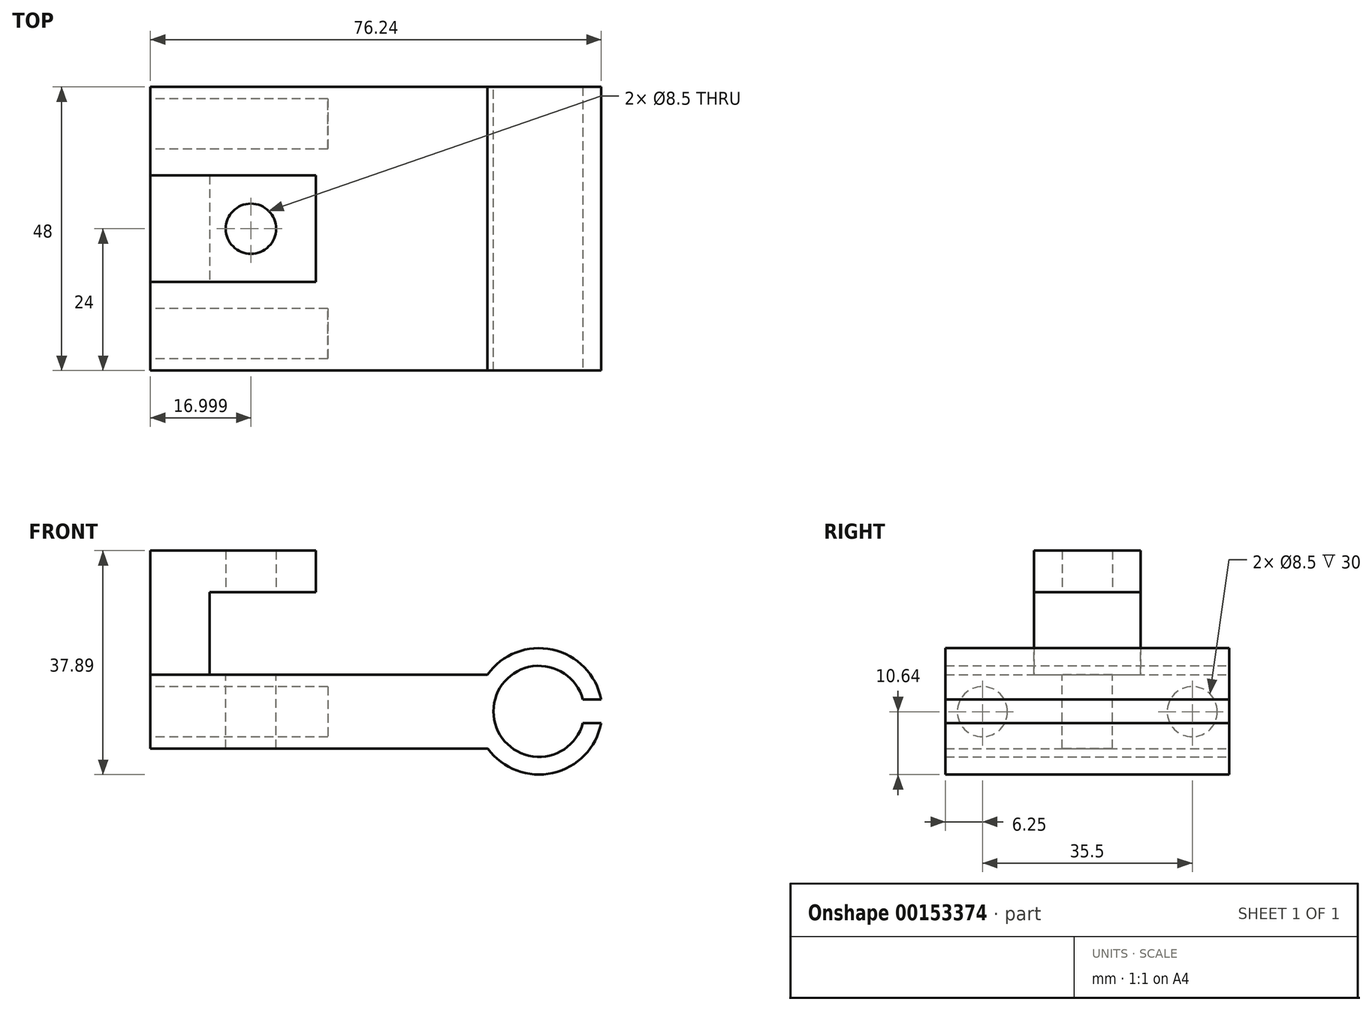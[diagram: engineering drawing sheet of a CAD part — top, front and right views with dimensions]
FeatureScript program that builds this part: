
annotation { "Feature Type Name" : "Feature", "Feature Type Description" : "" }
export const myFeature = defineFeature(function(context is Context, id is Id, definition is map)
    precondition{}
    {
        {
            assignVariable(context, id + "F0", {"name" : "LMXUU_L", "anyValue" : 24});
        }
        {
            assignVariable(context, id + "F1", {"name" : "ZZ_H", "anyValue" : 7});
        }
        {
            var Q0;
            Q0=qCreatedBy(makeId("Front.planeOp"),FACE);
            var sketch = newSketch(context, id + "F2", { "sketchPlane" : qUnion([Q0])});
            skLineSegment(sketch, "E0.bottom", {"start": v(0, 0) * mm, "end": v(-57.08, 0) * mm});
            skLineSegment(sketch, "E1", {"start": v(0, 0) * mm, "end": v(-0.08, 12.5) * mm});
            skCircle(sketch, "E2", {"center": v(8.64, 6.3) * mm, "radius": 7.7 * mm});
            skCircle(sketch, "E3", {"center": v(8.64, 6.3) * mm, "radius": 10.7 * mm});
            skLineSegment(sketch, "E4", {"start": v(-57.08, 0) * mm, "end": v(-57.08, 12.5) * mm});
            skLineSegment(sketch, "E5", {"start": v(-0.08, 12.5) * mm, "end": v(-57.08, 12.5) * mm});
            skSolve(sketch);
        }
        {
            var Q0;
            {var subQ0=sQuery(id+"F2.wireOp",EDGE,"E0.bottom");Q0=makeQuery(id+"F2.imprint","IMPRINT",FACE,{"disambiguationData":[TD([[makeQuery(id+"F2.imprint","IMPRINT",EDGE,{"derivedFrom":subQ0}),-1.0]])]});}
            var Q1;
            {var subQ0=sQuery(id+"F2.wireOp",EDGE,"E1");Q1=makeQuery(id+"F2.imprint","IMPRINT",FACE,{"disambiguationData":[TD([[makeQuery(id+"F2.imprint","IMPRINT",EDGE,{"derivedFrom":subQ0}),-1.0]])]});}
            var Q2;
            {var subQ0=sQuery(id+"F2.wireOp",EDGE,"E1");Q2=makeQuery(id+"F2.imprint","IMPRINT",FACE,{"disambiguationData":[TD([[makeQuery(id+"F2.imprint","IMPRINT",EDGE,{"derivedFrom":subQ0}),1.0]])]});}
            extrude(context, id + "F3", {"entities" : qUnion([Q0, Q1, Q2]), "depth" : (getVariable(context, 'LMXUU_L') * 2) * mm});
        }
        {
            var Q0;
            Q0=makeQuery(id+"F3.opExtrude","SWEPT_FACE",FACE,{"disambiguationData":[OSD([sQuery(id+"F2.wireOp",EDGE,"E4")])]});
            var sketch = newSketch(context, id + "F4", { "sketchPlane" : qUnion([Q0])});
            skCircle(sketch, "E6", {"center": v(6.25, 6.25) * mm, "radius": 4.25 * mm});
            skPoint(sketch, "E6.centerSnap0", {"position": v(0, 6.25) * mm});
            skCircle(sketch, "E7", {"center": v(41.75, 6.25) * mm, "radius": 4.25 * mm});
            skPoint(sketch, "E7.centerSnap0", {"position": v(48, 6.25) * mm});
            skSolve(sketch);
        }
        {
            var Q0;
            Q0=makeQuery(id+"F4.imprint","IMPRINT",FACE,{"disambiguationData":[TD([[makeQuery(id+"F4.imprint","IMPRINT",EDGE,{"derivedFrom":sQuery(id+"F4.wireOp",EDGE,"E6")}),1.0]])]});
            var Q1;
            Q1=makeQuery(id+"F4.imprint","IMPRINT",FACE,{"disambiguationData":[TD([[makeQuery(id+"F4.imprint","IMPRINT",EDGE,{"derivedFrom":sQuery(id+"F4.wireOp",EDGE,"E7")}),1.0]])]});
            extrude(context, id + "F5", {"entities" : qUnion([Q0, Q1]), "operationType" : NewBodyOperationType.REMOVE, "oppositeDirection" : true, "depth" : 30 * mm});
        }
        {
            var Q0;
            Q0=makeQuery(id+"F3.opExtrude","SWEPT_FACE",FACE,{"disambiguationData":[OSD([sQuery(id+"F2.wireOp",EDGE,"E5")])]});
            var sketch = newSketch(context, id + "F6", { "sketchPlane" : qUnion([Q0])});
            skLineSegment(sketch, "E8", {"start": v(-29.08, -24) * mm, "end": v(-29.08, -15) * mm, "construction": true});
            skLineSegment(sketch, "E9.bottom", {"start": v(-29.08, -15) * mm, "end": v(-57.08, -15) * mm});
            skLineSegment(sketch, "E9.top", {"start": v(-29.08, -33) * mm, "end": v(-57.08, -33) * mm});
            skLineSegment(sketch, "E9.left", {"start": v(-29.08, -15) * mm, "end": v(-29.08, -33) * mm});
            skLineSegment(sketch, "E9.right", {"start": v(-57.08, -15) * mm, "end": v(-57.08, -33) * mm});
            skCircle(sketch, "E10", {"center": v(-40.08, -24) * mm, "radius": 4.25 * mm});
            skSolve(sketch);
        }
        {
            var Q0;
            Q0=makeQuery(id+"F6.imprint","IMPRINT",FACE,{"disambiguationData":[TD([[makeQuery(id+"F6.imprint","IMPRINT",EDGE,{"derivedFrom":sQuery(id+"F6.wireOp",EDGE,"E9.bottom")}),1.0]])]});
            extrude(context, id + "F7", {"entities" : qUnion([Q0]), "depth" : ((getVariable(context, 'ZZ_H') * 2) + 7) * mm});
        }
        {
            var Q0;
            Q0=makeQuery(id+"F7.opExtrude","SWEPT_FACE",FACE,{"disambiguationData":[OSD([sQuery(id+"F6.wireOp",EDGE,"E9.top")])]});
            var sketch = newSketch(context, id + "F8", { "sketchPlane" : qUnion([Q0])});
            skLineSegment(sketch, "E11.bottom", {"start": v(-29.08, 12.5) * mm, "end": v(-47.08, 12.5) * mm});
            skLineSegment(sketch, "E11.top", {"start": v(-29.08, 26.5) * mm, "end": v(-47.08, 26.5) * mm});
            skLineSegment(sketch, "E11.left", {"start": v(-29.08, 12.5) * mm, "end": v(-29.08, 26.5) * mm});
            skLineSegment(sketch, "E11.right", {"start": v(-47.08, 12.5) * mm, "end": v(-47.08, 26.5) * mm});
            skSolve(sketch);
        }
        {
            var Q0;
            Q0=makeQuery(id+"F8.imprint","IMPRINT",FACE,{"disambiguationData":[TD([[makeQuery(id+"F8.imprint","IMPRINT",EDGE,{"derivedFrom":sQuery(id+"F8.wireOp",EDGE,"E11.bottom")}),-1.0]])]});
            extrude(context, id + "F9", {"entities" : qUnion([Q0]), "operationType" : NewBodyOperationType.REMOVE, "oppositeDirection" : true, "depth" : 25 * mm});
        }
        {
            var Q0;
            Q0=makeQuery(id+"F7.opExtrude","CAP_FACE",FACE,{"disambiguationData":[OSD([sQuery(id+"F6.wireOp",EDGE,"E9.bottom"),sQuery(id+"F6.wireOp",EDGE,"E9.top"),sQuery(id+"F6.wireOp",EDGE,"E9.left"),sQuery(id+"F6.wireOp",EDGE,"E9.right"),sQuery(id+"F6.wireOp",EDGE,"E10")])],"isStart":false});
            var sketch = newSketch(context, id + "F10", { "sketchPlane" : qUnion([Q0])});
            skCircle(sketch, "E12", {"center": v(-40.08, -24) * mm, "radius": 4.25 * mm});
            skSolve(sketch);
        }
        {
            var Q0;
            Q0 = qSketchRegion(id + "F10", true);
            extrude(context, id + "F11", {"entities" : qUnion([Q0]), "depth" : 25 * mm});
        }
        {
            var Q0;
            Q0=makeQuery(id+"F11.opExtrude","CAP_FACE",FACE,{"disambiguationData":[OSD([sQuery(id+"F10.wireOp",EDGE,"E12")])],"isStart":false});
            extrude(context, id + "F12", {"entities" : qUnion([Q0]), "operationType" : NewBodyOperationType.REMOVE, "oppositeDirection" : true, "depth" : 60 * mm});
        }
        {
            var Q0;
            Q0=makeQuery(id+"F3.opExtrude","CAP_FACE",FACE,{"disambiguationData":[OSD([sQuery(id+"F2.wireOp",EDGE,"E0.bottom"),sQuery(id+"F2.wireOp",EDGE,"E2"),sQuery(id+"F2.wireOp",EDGE,"E3"),sQuery(id+"F2.wireOp",EDGE,"E4"),sQuery(id+"F2.wireOp",EDGE,"E5")])],"isStart":false});
            var sketch = newSketch(context, id + "F13", { "sketchPlane" : qUnion([Q0])});
            skLineSegment(sketch, "E13", {"start": v(8.64, 6.3) * mm, "end": v(19.34, 6.3) * mm, "construction": true});
            skLineSegment(sketch, "E14", {"start": v(19.34, 6.3) * mm, "end": v(19.34, 8.3) * mm});
            skLineSegment(sketch, "E15", {"start": v(16.34, 6.3) * mm, "end": v(16.34, 4.3) * mm, "construction": true});
            skLineSegment(sketch, "E16.bottom", {"start": v(19.34, 8.3) * mm, "end": v(16.08, 8.3) * mm});
            skLineSegment(sketch, "E16.top", {"start": v(19.34, 4.3) * mm, "end": v(16.08, 4.3) * mm});
            skLineSegment(sketch, "E16.left", {"start": v(19.34, 8.3) * mm, "end": v(19.34, 4.3) * mm});
            skLineSegment(sketch, "E16.right", {"start": v(16.08, 8.3) * mm, "end": v(16.08, 4.3) * mm});
            skSolve(sketch);
        }
        {
            var Q0;
            {var subQ0=sQuery(id+"F13.wireOp",EDGE,"E16.bottom");var subQ1=makeQuery(id+"F3.opExtrude","CAP_EDGE",EDGE,{"disambiguationData":[OSD([sQuery(id+"F2.wireOp",EDGE,"E3")])],"isStart":false});var subQ2=makeQuery(id+"F13.imprint","INTERSECT",VERTEX,{"derivedFrom":[subQ1,subQ0]});Q0=makeQuery(id+"F13.imprint","IMPRINT",FACE,{"disambiguationData":[TD([[makeQuery(id+"F13.imprint","IMPRINT",EDGE,{"disambiguationData":[TD([[subQ2,1.0]])],"derivedFrom":subQ1}),1.0]])]});}
            var Q1;
            {var subQ0=sQuery(id+"F13.wireOp",EDGE,"E16.right");Q1=makeQuery(id+"F13.imprint","IMPRINT",FACE,{"disambiguationData":[TD([[makeQuery(id+"F13.imprint","IMPRINT",EDGE,{"derivedFrom":subQ0}),1.0]])]});}
            extrude(context, id + "F14", {"entities" : qUnion([Q0, Q1]), "operationType" : NewBodyOperationType.REMOVE, "oppositeDirection" : true, "depth" : (getVariable(context, 'LMXUU_L') * 2) * mm});
        }
    });
